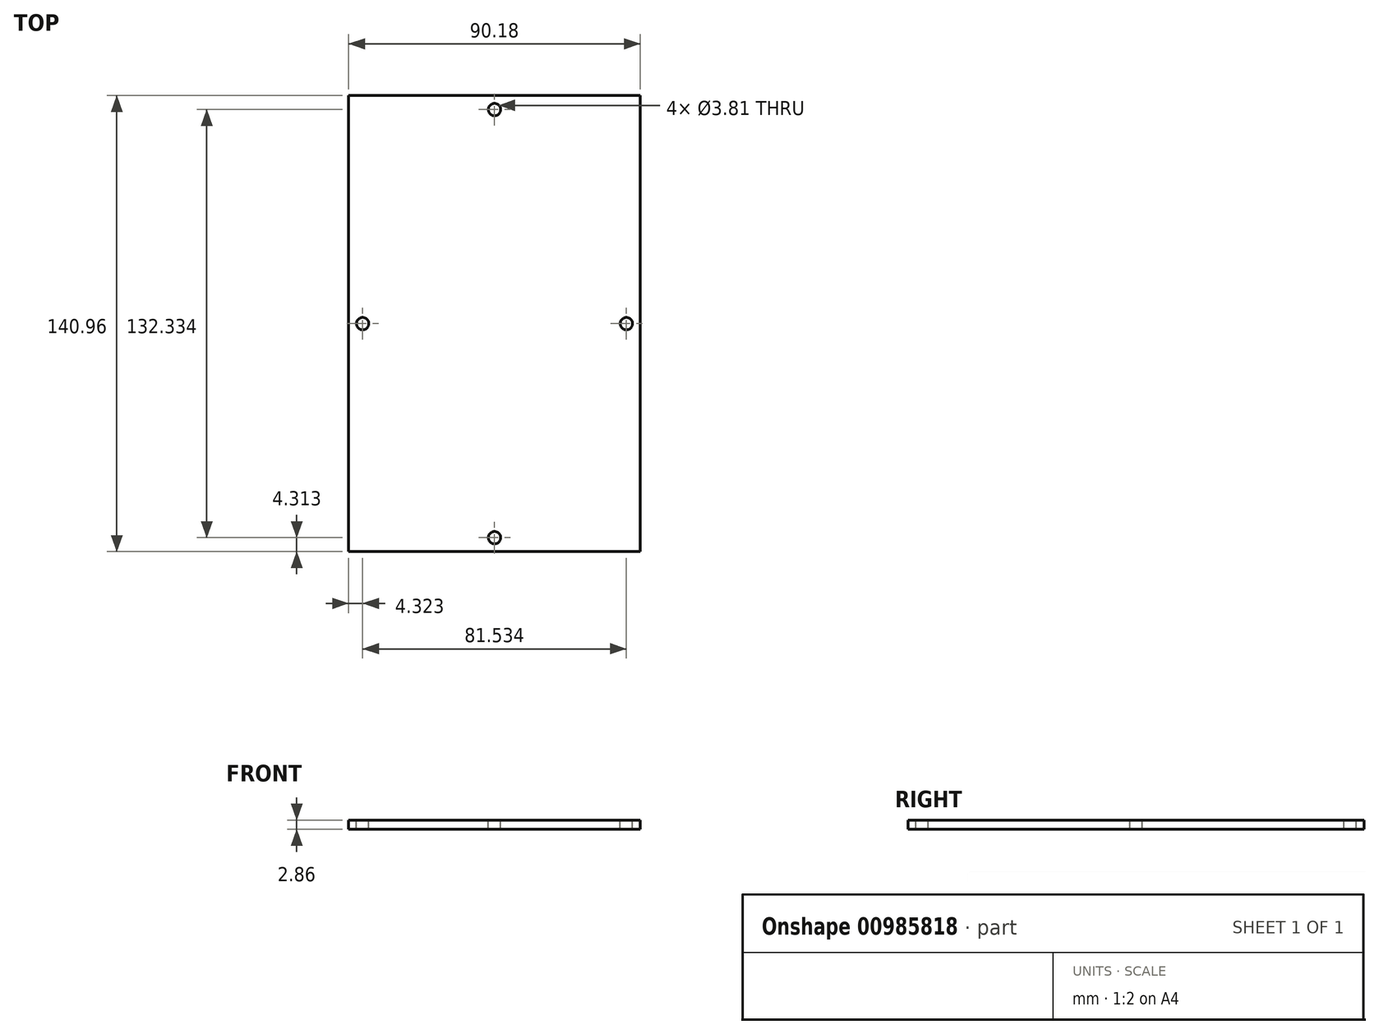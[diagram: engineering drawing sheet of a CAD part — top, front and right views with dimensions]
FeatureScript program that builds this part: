
annotation { "Feature Type Name" : "Feature", "Feature Type Description" : "" }
export const myFeature = defineFeature(function(context is Context, id is Id, definition is map)
    precondition{}
    {
        {
            var Q0;
            Q0=qCreatedBy(makeId("Top.planeOp"),FACE);
            var sketch = newSketch(context, id + "F0", { "sketchPlane" : qUnion([Q0])});
            skLineSegment(sketch, "E0.bottom", {"start": v(45.08, -70.48) * mm, "end": v(-45.09, -70.48) * mm});
            skLineSegment(sketch, "E0.top", {"start": v(45.09, 70.48) * mm, "end": v(-45.09, 70.48) * mm});
            skLineSegment(sketch, "E0.left", {"start": v(45.08, -70.48) * mm, "end": v(45.09, 70.49) * mm});
            skLineSegment(sketch, "E0.right", {"start": v(-45.09, -70.49) * mm, "end": v(-45.09, 70.48) * mm});
            skPoint(sketch, "E0.middle", {"position": v(0, 0) * mm});
            skSolve(sketch);
        }
        {
            var Q0;
            Q0 = qSketchRegion(id + "F0", true);
            extrude(context, id + "F1", {"entities" : qUnion([Q0]), "depth" : 2.86 * mm, "offsetDistance" : 25.4 * mm});
        }
        {
            var Q0;
            Q0=makeQuery(id+"F1.opExtrude","CAP_FACE",FACE,{"disambiguationData":[OSD([sQuery(id+"F0.wireOp",EDGE,"E0.bottom"),sQuery(id+"F0.wireOp",EDGE,"E0.top"),sQuery(id+"F0.wireOp",EDGE,"E0.left"),sQuery(id+"F0.wireOp",EDGE,"E0.right")])],"isStart":false});
            var sketch = newSketch(context, id + "F2", { "sketchPlane" : qUnion([Q0])});
            skCircle(sketch, "E1", {"center": v(0, -66.17) * mm, "radius": 1.9 * mm});
            skCircle(sketch, "E2", {"center": v(40.77, 0) * mm, "radius": 1.9 * mm});
            skCircle(sketch, "E3", {"center": v(0, 66.17) * mm, "radius": 1.9 * mm});
            skCircle(sketch, "E4", {"center": v(-40.77, 0) * mm, "radius": 1.9 * mm});
            skSolve(sketch);
        }
        {
            var Q0;
            Q0 = qSketchRegion(id + "F2", true);
            extrude(context, id + "F3", {"entities" : qUnion([Q0]), "operationType" : NewBodyOperationType.REMOVE, "oppositeDirection" : true, "depth" : 25.4 * mm, "offsetDistance" : 25.4 * mm});
        }
    });
